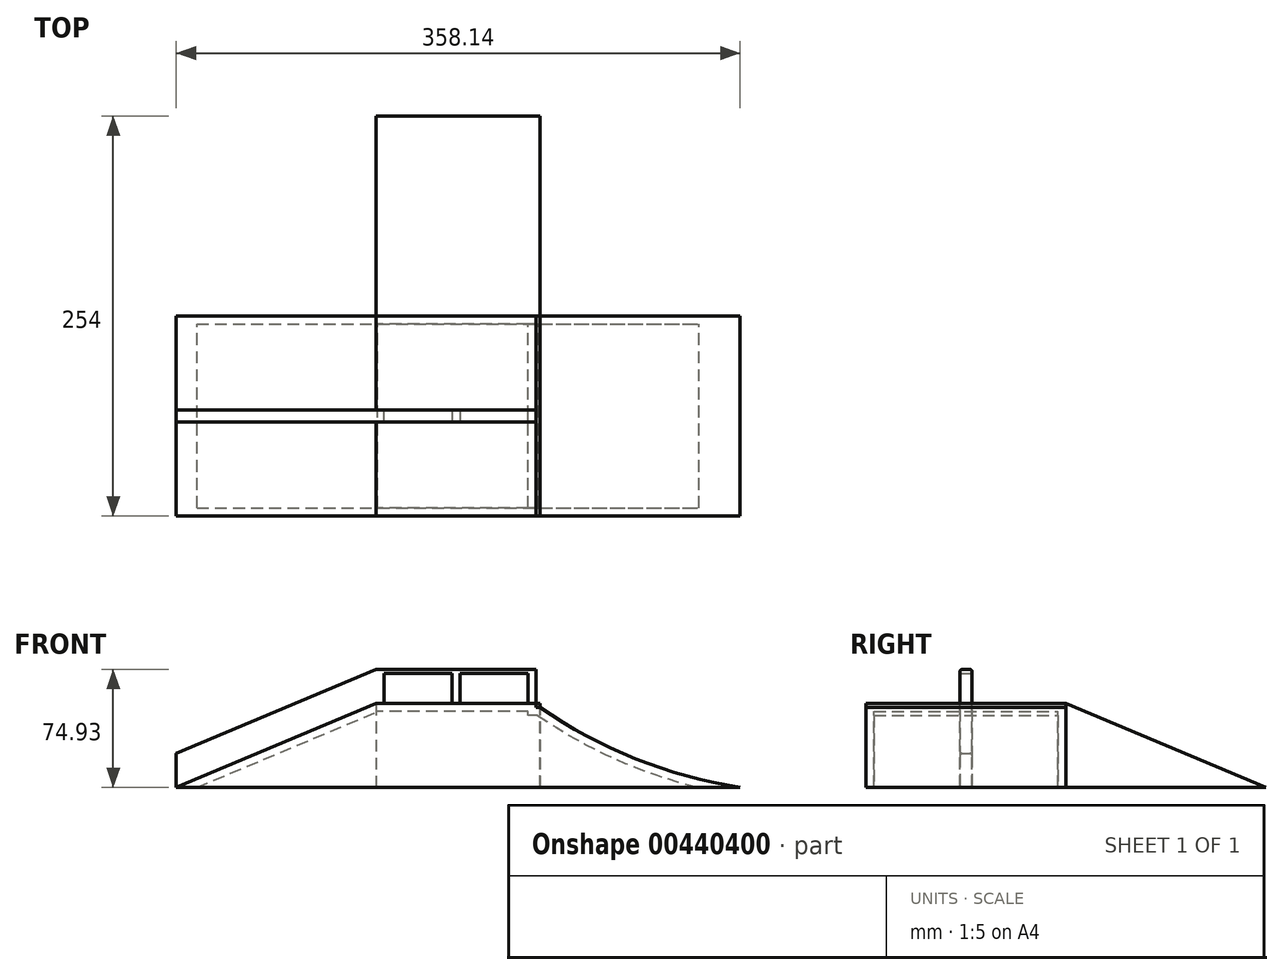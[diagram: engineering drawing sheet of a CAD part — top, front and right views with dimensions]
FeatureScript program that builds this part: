
annotation { "Feature Type Name" : "Feature", "Feature Type Description" : "" }
export const myFeature = defineFeature(function(context is Context, id is Id, definition is map)
    precondition{}
    {
        {
            var Q0;
            Q0=qCreatedBy(makeId("Front.planeOp"),FACE);
            var sketch = newSketch(context, id + "F0", { "sketchPlane" : qUnion([Q0])});
            skLineSegment(sketch, "E0.bottom", {"start": v(0, 0) * mm, "end": v(127, 0) * mm});
            skLineSegment(sketch, "E0.left", {"start": v(0, 0) * mm, "end": v(0, 50.8) * mm});
            skArc(sketch, "E1", {"start": v(0, 50.8) * mm, "mid": v(60.61, 18.18) * mm, "end": v(127, 0) * mm});
            skLineSegment(sketch, "E2.bottom", {"start": v(0, 0) * mm, "end": v(-2.54, 0) * mm});
            skLineSegment(sketch, "E2.top", {"start": v(0, 50.8) * mm, "end": v(-2.54, 50.8) * mm});
            skLineSegment(sketch, "E2.right", {"start": v(-2.54, 0) * mm, "end": v(-2.54, 50.8) * mm});
            skLineSegment(sketch, "E3.bottom", {"start": v(-2.54, 0) * mm, "end": v(-104.14, 0) * mm});
            skLineSegment(sketch, "E3.top", {"start": v(-2.54, 53.34) * mm, "end": v(-104.14, 53.34) * mm});
            skLineSegment(sketch, "E3.left", {"start": v(-2.54, 0) * mm, "end": v(-2.54, 53.34) * mm});
            skLineSegment(sketch, "E3.right", {"start": v(-104.14, 0) * mm, "end": v(-104.14, 53.34) * mm});
            skCircle(sketch, "E4", {"center": v(-1.27, 52.07) * mm, "radius": 1.27 * mm});
            skPoint(sketch, "E4.centerSnap0", {"position": v(-1.27, 50.8) * mm});
            skLineSegment(sketch, "E5", {"start": v(-104.14, 0) * mm, "end": v(-231.14, 0) * mm});
            skLineSegment(sketch, "E6", {"start": v(-231.14, 0) * mm, "end": v(-104.14, 53.34) * mm});
            skSolve(sketch);
        }
        {
            var Q0;
            Q0=makeQuery(id+"F0.imprint","IMPRINT",FACE,{"disambiguationData":[TD([[makeQuery(id+"F0.imprint","IMPRINT",EDGE,{"derivedFrom":sQuery(id+"F0.wireOp",EDGE,"E0.bottom")}),1.0]])]});
            var Q1;
            Q1=makeQuery(id+"F0.imprint","IMPRINT",FACE,{"disambiguationData":[TD([[makeQuery(id+"F0.imprint","IMPRINT",EDGE,{"derivedFrom":sQuery(id+"F0.wireOp",EDGE,"gSf4ow2M-3nON-57kk-JyT3-ZSVy4p9OPfto.bottom")}),-1.0]])]});
            var Q2;
            {var subQ3=sQuery(id+"F0.wireOp",EDGE,"E3.bottom");Q2=makeQuery(id+"F0.imprint","IMPRINT",FACE,{"disambiguationData":[TD([[makeQuery(id+"F0.imprint","IMPRINT",EDGE,{"derivedFrom":subQ3}),-1.0]])]});}
            var Q3;
            {var subQ5=sQuery(id+"F0.wireOp",EDGE,"E2.bottom");Q3=makeQuery(id+"F0.imprint","IMPRINT",FACE,{"disambiguationData":[TD([[makeQuery(id+"F0.imprint","IMPRINT",EDGE,{"derivedFrom":subQ5}),-1.0]])]});}
            var Q4;
            {var subQ0=sQuery(id+"F0.wireOp",EDGE,"E4");var subQ1=makeQuery(id+"F0.imprint","INTERSECT",VERTEX,{"derivedFrom":[sQuery(id+"F0.wireOp",EDGE,"E2.top"),subQ0]});Q4=makeQuery(id+"F0.imprint","IMPRINT",FACE,{"disambiguationData":[TD([[makeQuery(id+"F0.imprint","IMPRINT",EDGE,{"disambiguationData":[TD([[subQ1,1.0]])],"derivedFrom":subQ0}),1.0]])]});}
            var Q5;
            Q5=makeQuery(id+"F0.imprint","IMPRINT",FACE,{"disambiguationData":[TD([[makeQuery(id+"F0.imprint","IMPRINT",EDGE,{"derivedFrom":sQuery(id+"F0.wireOp",EDGE,"E3.right")}),1.0]])]});
            extrude(context, id + "F1", {"entities" : qUnion([Q0, Q1, Q2, Q3, Q4, Q5]), "depth" : 127 * mm});
        }
        {
            var Q0;
            Q0=makeQuery(id+"F1.opExtrude","SWEPT_FACE",FACE,{"disambiguationData":[OSD([sQuery(id+"F0.wireOp",EDGE,"E3.top")])]});
            var sketch = newSketch(context, id + "F2", { "sketchPlane" : qUnion([Q0])});
            skLineSegment(sketch, "E7.bottom", {"start": v(-104.14, -67.31) * mm, "end": v(-99.06, -67.31) * mm});
            skLineSegment(sketch, "E7.top", {"start": v(-104.14, -59.7) * mm, "end": v(-99.06, -59.7) * mm});
            skLineSegment(sketch, "E7.left", {"start": v(-104.14, -67.31) * mm, "end": v(-104.14, -59.7) * mm});
            skLineSegment(sketch, "E7.right", {"start": v(-99.06, -67.31) * mm, "end": v(-99.06, -59.7) * mm});
            skLineSegment(sketch, "E8.bottom", {"start": v(-2.54, -67.3) * mm, "end": v(-7.62, -67.3) * mm});
            skLineSegment(sketch, "E8.top", {"start": v(-2.54, -59.7) * mm, "end": v(-7.62, -59.7) * mm});
            skLineSegment(sketch, "E8.left", {"start": v(-2.54, -67.3) * mm, "end": v(-2.54, -59.7) * mm});
            skLineSegment(sketch, "E8.right", {"start": v(-7.62, -67.3) * mm, "end": v(-7.62, -59.7) * mm});
            skLineSegment(sketch, "E9.bottom", {"start": v(-55.88, -59.7) * mm, "end": v(-50.8, -59.7) * mm});
            skLineSegment(sketch, "E9.top", {"start": v(-55.88, -67.31) * mm, "end": v(-50.8, -67.31) * mm});
            skLineSegment(sketch, "E9.left", {"start": v(-55.88, -59.7) * mm, "end": v(-55.88, -67.31) * mm});
            skLineSegment(sketch, "E9.right", {"start": v(-50.8, -59.7) * mm, "end": v(-50.8, -67.31) * mm});
            skSolve(sketch);
        }
        {
            var Q0;
            Q0 = qSketchRegion(id + "F2", true);
            extrude(context, id + "F3", {"entities" : qUnion([Q0]), "operationType" : NewBodyOperationType.ADD, "depth" : 19.05 * mm, "offsetDistance" : 25.4 * mm});
        }
        {
            var Q0;
            Q0=makeQuery(id+"F3.boolean.opBoolean","MERGE",FACE,{"derivedFrom":[makeQuery(id+"F1.opExtrude","SWEPT_FACE",FACE,{"disambiguationData":[OSD([sQuery(id+"F0.wireOp",EDGE,"E3.left")])]}),makeQuery(id+"F3.opExtrude","SWEPT_FACE",FACE,{"disambiguationData":[OSD([sQuery(id+"F2.wireOp",EDGE,"E8.left")])]})]});
            var sketch = newSketch(context, id + "F4", { "sketchPlane" : qUnion([Q0])});
            skLineSegment(sketch, "E10.bottom", {"start": v(-67.3, 72.4) * mm, "end": v(-59.7, 72.4) * mm});
            skLineSegment(sketch, "E10.top", {"start": v(-67.3, 74.93) * mm, "end": v(-59.7, 74.93) * mm});
            skLineSegment(sketch, "E10.left", {"start": v(-67.3, 72.4) * mm, "end": v(-67.3, 74.93) * mm});
            skLineSegment(sketch, "E10.right", {"start": v(-59.7, 72.4) * mm, "end": v(-59.7, 74.93) * mm});
            skSolve(sketch);
        }
        {
            var Q0;
            Q0=makeQuery(id+"F4.imprint","IMPRINT",FACE,{"disambiguationData":[TD([[makeQuery(id+"F4.imprint","IMPRINT",EDGE,{"derivedFrom":sQuery(id+"F4.wireOp",EDGE,"E10.bottom")}),1.0]])]});
            extrude(context, id + "F5", {"entities" : qUnion([Q0]), "operationType" : NewBodyOperationType.ADD, "oppositeDirection" : true, "depth" : 101.6 * mm});
        }
        {
            var Q0;
            Q0=makeQuery(id+"F1.opExtrude","SWEPT_FACE",FACE,{"disambiguationData":[OSD([sQuery(id+"F0.wireOp",EDGE,"E0.bottom"),sQuery(id+"F0.wireOp",EDGE,"E2.bottom"),sQuery(id+"F0.wireOp",EDGE,"E3.bottom"),sQuery(id+"F0.wireOp",EDGE,"E5")])]});
            shell(context, id + "F6", {"entities" : qUnion([Q0]), "thickness" : 5.08 * mm});
        }
        {
            var Q0;
            Q0=makeQuery(id+"F5.boolean.opBoolean","MERGE",FACE,{"derivedFrom":[makeQuery(id+"F3.opExtrude","SWEPT_FACE",FACE,{"disambiguationData":[OSD([sQuery(id+"F2.wireOp",EDGE,"E7.top")])]}),makeQuery(id+"F3.opExtrude","SWEPT_FACE",FACE,{"disambiguationData":[OSD([sQuery(id+"F2.wireOp",EDGE,"E8.top")])]}),makeQuery(id+"F3.opExtrude","SWEPT_FACE",FACE,{"disambiguationData":[OSD([sQuery(id+"F2.wireOp",EDGE,"E9.bottom")])]}),makeQuery(id+"F5.opExtrude","SWEPT_FACE",FACE,{"disambiguationData":[OSD([sQuery(id+"F4.wireOp",EDGE,"E10.right")])]})]});
            var sketch = newSketch(context, id + "F7", { "sketchPlane" : qUnion([Q0])});
            skLineSegment(sketch, "E11", {"start": v(104.14, 74.93) * mm, "end": v(231.14, 21.59) * mm});
            skLineSegment(sketch, "E12", {"start": v(231.14, 21.59) * mm, "end": v(231.14, 0) * mm});
            skLineSegment(sketch, "E13", {"start": v(231.14, 0) * mm, "end": v(104.14, 53.34) * mm});
            skLineSegment(sketch, "E14", {"start": v(104.14, 74.93) * mm, "end": v(104.14, 53.34) * mm});
            skSolve(sketch);
        }
        {
            var Q0;
            Q0 = qSketchRegion(id + "F7", true);
            extrude(context, id + "F8", {"entities" : qUnion([Q0]), "operationType" : NewBodyOperationType.ADD, "oppositeDirection" : true, "depth" : 7.62 * mm});
        }
        {
            var Q0;
            Q0=qCreatedBy(makeId("Right.planeOp"),FACE);
            var sketch = newSketch(context, id + "F9", { "sketchPlane" : qUnion([Q0])});
            skLineSegment(sketch, "E15", {"start": v(0, 53.34) * mm, "end": v(127, 0) * mm});
            skLineSegment(sketch, "E16", {"start": v(127, 0) * mm, "end": v(0, 0) * mm});
            skLineSegment(sketch, "E17", {"start": v(0, 0) * mm, "end": v(0, 53.34) * mm});
            skSolve(sketch);
        }
        {
            var Q0;
            Q0=makeQuery(id+"F9.imprint","IMPRINT",FACE,{"disambiguationData":[TD([[makeQuery(id+"F9.imprint","IMPRINT",EDGE,{"derivedFrom":sQuery(id+"F9.wireOp",EDGE,"E15")}),-1.0]])]});
            extrude(context, id + "F10", {"entities" : qUnion([Q0]), "oppositeDirection" : true, "depth" : 104.14 * mm});
        }
        {
            var Q0;
            Q0=makeQuery(id+"F5.opExtrude","SWEPT_EDGE",EDGE,{"disambiguationData":[OSD([sQuery(id+"F4.wireOp",EDGE,"E10.top"),sQuery(id+"F4.wireOp",EDGE,"E10.left")])]});
            var Q1;
            Q1=makeQuery(id+"F8.opExtrude","CAP_EDGE",EDGE,{"disambiguationData":[OSD([sQuery(id+"F7.wireOp",EDGE,"E11")])],"isStart":false});
            var Q2;
            {var subQ0=sQuery(id+"F4.wireOp",EDGE,"E10.top");Q2=makeQuery(id+"F8.boolean.opBoolean","MERGE",EDGE,{"derivedFrom":[makeQuery(id+"F5.opExtrude","CAP_EDGE",EDGE,{"disambiguationData":[OSD([subQ0])],"isStart":false}),makeQuery(id+"F8.opExtrude","SWEPT_EDGE",EDGE,{"disambiguationData":[OSD([subQ0,sQuery(id+"F4.wireOp",EDGE,"E10.right"),sQuery(id+"F7.wireOp",EDGE,"E11"),sQuery(id+"F7.wireOp",EDGE,"E14")])]})]});}
            var Q3;
            Q3=makeQuery(id+"F8.opExtrude","CAP_EDGE",EDGE,{"disambiguationData":[OSD([sQuery(id+"F7.wireOp",EDGE,"E11")])],"isStart":true});
            var Q4;
            Q4=makeQuery(id+"F5.opExtrude","SWEPT_EDGE",EDGE,{"disambiguationData":[OSD([sQuery(id+"F4.wireOp",EDGE,"E10.top"),sQuery(id+"F4.wireOp",EDGE,"E10.right")])]});
            fillet(context, id + "F11", {"entities" : qUnion([Q0, Q1, Q2, Q3, Q4]), "radius" : 1.27 * mm, "tangentPropagation" : true, "allowEdgeOverflow" : false});
        }
    });
